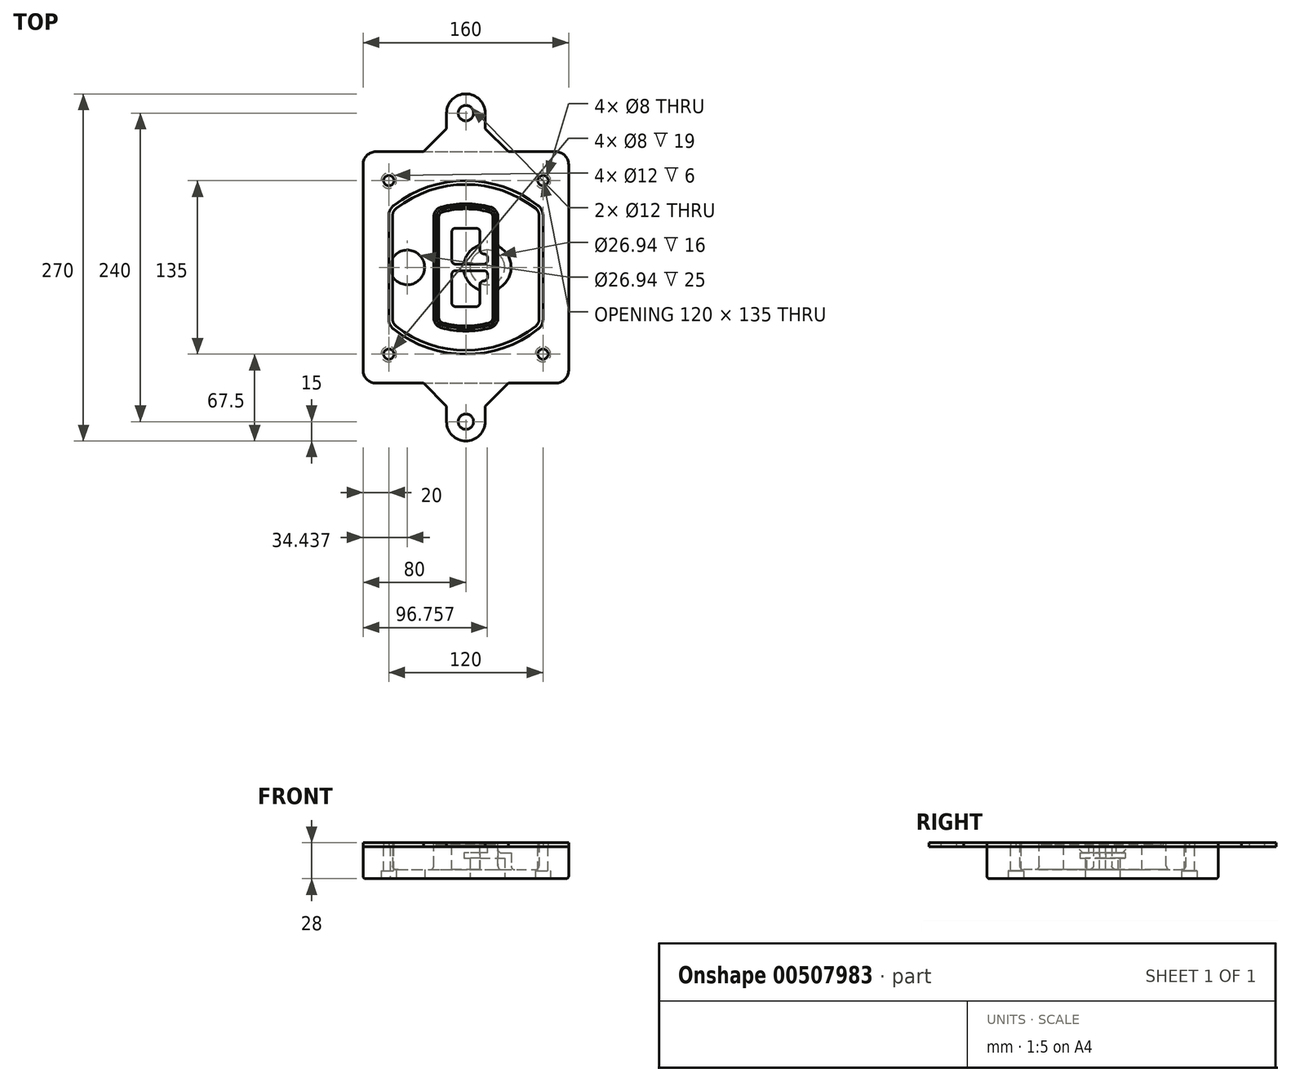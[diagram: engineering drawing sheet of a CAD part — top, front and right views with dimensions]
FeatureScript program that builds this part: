
annotation { "Feature Type Name" : "Feature", "Feature Type Description" : "" }
export const myFeature = defineFeature(function(context is Context, id is Id, definition is map)
    precondition{}
    {
        {
            var Q0;
            Q0=qCreatedBy(makeId("Top.planeOp"),FACE);
            var sketch = newSketch(context, id + "F0", { "sketchPlane" : qUnion([Q0])});
            skPoint(sketch, "E0.rect.middle", {"position": v(0, 0) * mm});
            skLineSegment(sketch, "E1.bottom", {"start": v(-70, -90) * mm, "end": v(70, -90) * mm});
            skLineSegment(sketch, "E1.top", {"start": v(-70, 90) * mm, "end": v(70, 90) * mm});
            skLineSegment(sketch, "E1.left", {"start": v(-80, -80) * mm, "end": v(-80, 80) * mm});
            skLineSegment(sketch, "E1.right", {"start": v(80, -80) * mm, "end": v(80, 80) * mm});
            skLineSegment(sketch, "E2", {"start": v(-80, 90) * mm, "end": v(80, -90) * mm, "construction": true});
            skLineSegment(sketch, "E3", {"start": v(80, 90) * mm, "end": v(-80, -90) * mm, "construction": true});
            skCircle(sketch, "E4", {"center": v(-60, 67.5) * mm, "radius": 4 * mm});
            skCircle(sketch, "E5", {"center": v(60, 67.5) * mm, "radius": 4 * mm});
            skCircle(sketch, "E6", {"center": v(60, -67.5) * mm, "radius": 4 * mm});
            skCircle(sketch, "E7", {"center": v(-60, -67.5) * mm, "radius": 4 * mm});
            skLineSegment(sketch, "E8", {"start": v(-60, 67.5) * mm, "end": v(60, 67.5) * mm, "construction": true});
            skLineSegment(sketch, "E9", {"start": v(60, 67.5) * mm, "end": v(60, -67.5) * mm, "construction": true});
            skLineSegment(sketch, "E10", {"start": v(60, -67.5) * mm, "end": v(-60, -67.5) * mm, "construction": true});
            skLineSegment(sketch, "E11", {"start": v(-60, -67.5) * mm, "end": v(-60, 67.5) * mm, "construction": true});
            skLineSegment(sketch, "E12", {"start": v(-60, 40.3) * mm, "end": v(-60, -40.3) * mm});
            skLineSegment(sketch, "E13", {"start": v(60, 40.3) * mm, "end": v(60, -40.3) * mm});
            skArc(sketch, "E14", {"start": v(56.15, 48.18) * mm, "mid": v(0, 67.5) * mm, "end": v(-56.15, 48.18) * mm});
            skArc(sketch, "E15", {"start": v(-56.15, -48.18) * mm, "mid": v(0, -67.5) * mm, "end": v(56.15, -48.18) * mm});
            skLineSegment(sketch, "E16", {"start": v(-60, 0) * mm, "end": v(60, 0) * mm, "construction": true});
            skPoint(sketch, "E17.visualSharp", {"position": v(-60, -45) * mm});
            skArc(sketch, "E17.filletArc", {"start": v(-60, -40.3) * mm, "mid": v(-58.99, -44.68) * mm, "end": v(-56.15, -48.18) * mm});
            skPoint(sketch, "E18.visualSharp", {"position": v(-60, 45) * mm});
            skArc(sketch, "E18.filletArc", {"start": v(-56.15, 48.18) * mm, "mid": v(-58.99, 44.68) * mm, "end": v(-60, 40.3) * mm});
            skPoint(sketch, "E19.visualSharp", {"position": v(60, 45) * mm});
            skArc(sketch, "E19.filletArc", {"start": v(60, 40.3) * mm, "mid": v(58.99, 44.68) * mm, "end": v(56.15, 48.18) * mm});
            skPoint(sketch, "E20.visualSharp", {"position": v(60, -45) * mm});
            skArc(sketch, "E20.filletArc", {"start": v(56.15, -48.18) * mm, "mid": v(58.99, -44.68) * mm, "end": v(60, -40.3) * mm});
            skPoint(sketch, "E21.visualSharp", {"position": v(-80, 90) * mm});
            skArc(sketch, "E21.filletArc", {"start": v(-70, 90) * mm, "mid": v(-77.07, 87.07) * mm, "end": v(-80, 80) * mm});
            skPoint(sketch, "E22.visualSharp", {"position": v(80, 90) * mm});
            skArc(sketch, "E22.filletArc", {"start": v(80, 80) * mm, "mid": v(77.07, 87.07) * mm, "end": v(70, 90) * mm});
            skPoint(sketch, "E23.visualSharp", {"position": v(80, -90) * mm});
            skArc(sketch, "E23.filletArc", {"start": v(70, -90) * mm, "mid": v(77.07, -87.07) * mm, "end": v(80, -80) * mm});
            skPoint(sketch, "E24.visualSharp", {"position": v(-80, -90) * mm});
            skArc(sketch, "E24.filletArc", {"start": v(-80, -80) * mm, "mid": v(-77.07, -87.07) * mm, "end": v(-70, -90) * mm});
            skArc(sketch, "E25.0", {"start": v(57, 40.3) * mm, "mid": v(56.3, 43.36) * mm, "end": v(54.3, 45.81) * mm});
            skLineSegment(sketch, "E25.1", {"start": v(57, 40.3) * mm, "end": v(57, -40.3) * mm});
            skArc(sketch, "E25.2", {"start": v(54.3, -45.81) * mm, "mid": v(56.3, -43.36) * mm, "end": v(57, -40.3) * mm});
            skArc(sketch, "E25.3", {"start": v(-54.3, -45.81) * mm, "mid": v(0, -64.5) * mm, "end": v(54.3, -45.81) * mm});
            skArc(sketch, "E25.4", {"start": v(-57, -40.3) * mm, "mid": v(-56.3, -43.36) * mm, "end": v(-54.3, -45.81) * mm});
            skArc(sketch, "E25.5", {"start": v(54.3, 45.81) * mm, "mid": v(0, 64.5) * mm, "end": v(-54.3, 45.81) * mm});
            skLineSegment(sketch, "E25.6", {"start": v(-57, 40.3) * mm, "end": v(-57, -40.3) * mm});
            skArc(sketch, "E25.7", {"start": v(-54.3, 45.81) * mm, "mid": v(-56.3, 43.36) * mm, "end": v(-57, 40.3) * mm});
            skArc(sketch, "E26.0", {"start": v(-58.62, 51.33) * mm, "mid": v(-62.58, 46.43) * mm, "end": v(-64, 40.3) * mm});
            skArc(sketch, "E26.1", {"start": v(58.62, 51.33) * mm, "mid": v(0, 71.5) * mm, "end": v(-58.62, 51.33) * mm});
            skArc(sketch, "E26.2", {"start": v(64, 40.3) * mm, "mid": v(62.58, 46.43) * mm, "end": v(58.62, 51.33) * mm});
            skLineSegment(sketch, "E26.3", {"start": v(64, 40.3) * mm, "end": v(64, -40.3) * mm});
            skArc(sketch, "E26.4", {"start": v(58.62, -51.33) * mm, "mid": v(62.58, -46.43) * mm, "end": v(64, -40.3) * mm});
            skLineSegment(sketch, "E26.5", {"start": v(-64, 40.3) * mm, "end": v(-64, -40.3) * mm});
            skArc(sketch, "E26.6", {"start": v(-58.62, -51.33) * mm, "mid": v(0, -71.5) * mm, "end": v(58.62, -51.33) * mm});
            skArc(sketch, "E26.7", {"start": v(-64, -40.3) * mm, "mid": v(-62.58, -46.43) * mm, "end": v(-58.62, -51.33) * mm});
            skSolve(sketch);
        }
        {
            var Q0;
            Q0=makeQuery(id+"F0.imprint","IMPRINT",FACE,{"disambiguationData":[TD([[makeQuery(id+"F0.imprint","IMPRINT",EDGE,{"derivedFrom":sQuery(id+"F0.wireOp",EDGE,"E1.bottom")}),1.0]])]});
            var Q1;
            Q1=makeQuery(id+"F0.imprint","IMPRINT",FACE,{"disambiguationData":[TD([[makeQuery(id+"F0.imprint","IMPRINT",EDGE,{"derivedFrom":sQuery(id+"F0.wireOp",EDGE,"E12")}),1.0]])]});
            var Q2;
            Q2=makeQuery(id+"F0.imprint","IMPRINT",FACE,{"disambiguationData":[TD([[makeQuery(id+"F0.imprint","IMPRINT",EDGE,{"derivedFrom":sQuery(id+"F0.wireOp",EDGE,"E25.0")}),1.0]])]});
            var Q3;
            Q3=makeQuery(id+"F0.imprint","IMPRINT",FACE,{"disambiguationData":[TD([[makeQuery(id+"F0.imprint","IMPRINT",EDGE,{"derivedFrom":sQuery(id+"F0.wireOp",EDGE,"E12")}),-1.0]])]});
            extrude(context, id + "F1", {"entities" : qUnion([Q0, Q1, Q2, Q3]), "oppositeDirection" : true, "depth" : 25 * mm});
        }
        {
            var Q0;
            Q0=makeQuery(id+"F0.imprint","IMPRINT",FACE,{"disambiguationData":[TD([[makeQuery(id+"F0.imprint","IMPRINT",EDGE,{"derivedFrom":sQuery(id+"F0.wireOp",EDGE,"E12")}),1.0]])]});
            extrude(context, id + "F2", {"entities" : qUnion([Q0]), "operationType" : NewBodyOperationType.ADD, "depth" : 3 * mm});
        }
        {
            var Q0;
            Q0=makeQuery(id+"F0.imprint","IMPRINT",FACE,{"disambiguationData":[TD([[makeQuery(id+"F0.imprint","IMPRINT",EDGE,{"derivedFrom":sQuery(id+"F0.wireOp",EDGE,"E25.0")}),1.0]])]});
            extrude(context, id + "F3", {"entities" : qUnion([Q0]), "operationType" : NewBodyOperationType.REMOVE, "oppositeDirection" : true, "depth" : 18 * mm});
        }
        {
            var Q0;
            Q0=makeQuery(id+"F2.opExtrude","CAP_FACE",FACE,{"disambiguationData":[OSD([sQuery(id+"F0.wireOp",EDGE,"E12"),sQuery(id+"F0.wireOp",EDGE,"E13"),sQuery(id+"F0.wireOp",EDGE,"E14"),sQuery(id+"F0.wireOp",EDGE,"E15"),sQuery(id+"F0.wireOp",EDGE,"E17.filletArc"),sQuery(id+"F0.wireOp",EDGE,"E18.filletArc"),sQuery(id+"F0.wireOp",EDGE,"E19.filletArc"),sQuery(id+"F0.wireOp",EDGE,"E20.filletArc"),sQuery(id+"F0.wireOp",EDGE,"E25.0"),sQuery(id+"F0.wireOp",EDGE,"E25.1"),sQuery(id+"F0.wireOp",EDGE,"E25.2"),sQuery(id+"F0.wireOp",EDGE,"E25.3"),sQuery(id+"F0.wireOp",EDGE,"E25.4"),sQuery(id+"F0.wireOp",EDGE,"E25.5"),sQuery(id+"F0.wireOp",EDGE,"E25.6"),sQuery(id+"F0.wireOp",EDGE,"E25.7")])],"isStart":false});
            var sketch = newSketch(context, id + "F4", { "sketchPlane" : qUnion([Q0])});
            skArc(sketch, "E27.0", {"start": v(-19.08, -46.97) * mm, "mid": v(0, -49.5) * mm, "end": v(19.08, -46.97) * mm});
            skArc(sketch, "E28.0", {"start": v(19.08, 46.97) * mm, "mid": v(0, 49.5) * mm, "end": v(-19.08, 46.97) * mm});
            skLineSegment(sketch, "E29", {"start": v(-25, 39.25) * mm, "end": v(-25, -39.25) * mm});
            skLineSegment(sketch, "E30", {"start": v(25, 39.25) * mm, "end": v(25, -39.25) * mm});
            skLineSegment(sketch, "E31", {"start": v(-25, 45.1) * mm, "end": v(25, 45.1) * mm, "construction": true});
            skLineSegment(sketch, "E32", {"start": v(-25, -45.1) * mm, "end": v(25, -45.1) * mm, "construction": true});
            skPoint(sketch, "E33.visualSharp", {"position": v(-25, 45.1) * mm});
            skArc(sketch, "E33.filletArc", {"start": v(-19.08, 46.97) * mm, "mid": v(-23.35, 44.11) * mm, "end": v(-25, 39.25) * mm});
            skPoint(sketch, "E34.visualSharp", {"position": v(25, 45.1) * mm});
            skArc(sketch, "E34.filletArc", {"start": v(25, 39.25) * mm, "mid": v(23.35, 44.11) * mm, "end": v(19.08, 46.97) * mm});
            skPoint(sketch, "E35.visualSharp", {"position": v(25, -45.1) * mm});
            skArc(sketch, "E35.filletArc", {"start": v(19.08, -46.97) * mm, "mid": v(23.35, -44.11) * mm, "end": v(25, -39.25) * mm});
            skPoint(sketch, "E36.visualSharp", {"position": v(-25, -45.1) * mm});
            skArc(sketch, "E36.filletArc", {"start": v(-25, -39.25) * mm, "mid": v(-23.35, -44.11) * mm, "end": v(-19.08, -46.97) * mm});
            skArc(sketch, "E37.0", {"start": v(54.3, 45.81) * mm, "mid": v(0, 64.5) * mm, "end": v(-54.3, 45.81) * mm});
            skArc(sketch, "E37.1", {"start": v(-54.3, 45.81) * mm, "mid": v(-56.3, 43.36) * mm, "end": v(-57, 40.3) * mm});
            skLineSegment(sketch, "E37.2", {"start": v(-57, 40.3) * mm, "end": v(-57, -40.3) * mm});
            skArc(sketch, "E37.3", {"start": v(-57, -40.3) * mm, "mid": v(-56.3, -43.36) * mm, "end": v(-54.3, -45.81) * mm});
            skArc(sketch, "E37.4", {"start": v(-54.3, -45.81) * mm, "mid": v(0, -64.5) * mm, "end": v(54.3, -45.81) * mm});
            skArc(sketch, "E37.5", {"start": v(54.3, -45.81) * mm, "mid": v(56.3, -43.36) * mm, "end": v(57, -40.3) * mm});
            skLineSegment(sketch, "E37.6", {"start": v(57, 40.3) * mm, "end": v(57, -40.3) * mm});
            skArc(sketch, "E37.7", {"start": v(57, 40.3) * mm, "mid": v(56.3, 43.36) * mm, "end": v(54.3, 45.81) * mm});
            skLineSegment(sketch, "E38.0", {"start": v(23, 39.25) * mm, "end": v(23, -39.25) * mm});
            skArc(sketch, "E38.1", {"start": v(18.56, -45.04) * mm, "mid": v(21.76, -42.9) * mm, "end": v(23, -39.25) * mm});
            skArc(sketch, "E38.2", {"start": v(-18.56, -45.04) * mm, "mid": v(0, -47.5) * mm, "end": v(18.56, -45.04) * mm});
            skArc(sketch, "E38.3", {"start": v(-23, -39.25) * mm, "mid": v(-21.76, -42.9) * mm, "end": v(-18.56, -45.04) * mm});
            skLineSegment(sketch, "E38.4", {"start": v(-23, 39.25) * mm, "end": v(-23, -39.25) * mm});
            skArc(sketch, "E38.5", {"start": v(23, 39.25) * mm, "mid": v(21.76, 42.9) * mm, "end": v(18.56, 45.04) * mm});
            skArc(sketch, "E38.6", {"start": v(-18.56, 45.04) * mm, "mid": v(-21.76, 42.9) * mm, "end": v(-23, 39.25) * mm});
            skArc(sketch, "E38.7", {"start": v(18.56, 45.04) * mm, "mid": v(0, 47.5) * mm, "end": v(-18.56, 45.04) * mm});
            skArc(sketch, "E39.0", {"start": v(21, 39.25) * mm, "mid": v(20.18, 41.68) * mm, "end": v(18.04, 43.1) * mm});
            skLineSegment(sketch, "E39.1", {"start": v(21, 39.25) * mm, "end": v(21, -39.25) * mm});
            skArc(sketch, "E39.2", {"start": v(18.04, -43.1) * mm, "mid": v(20.18, -41.68) * mm, "end": v(21, -39.25) * mm});
            skArc(sketch, "E39.3", {"start": v(-18.04, -43.1) * mm, "mid": v(0, -45.5) * mm, "end": v(18.04, -43.1) * mm});
            skArc(sketch, "E39.4", {"start": v(-21, -39.25) * mm, "mid": v(-20.18, -41.68) * mm, "end": v(-18.04, -43.1) * mm});
            skArc(sketch, "E39.5", {"start": v(18.04, 43.1) * mm, "mid": v(0, 45.5) * mm, "end": v(-18.04, 43.1) * mm});
            skLineSegment(sketch, "E39.6", {"start": v(-21, 39.25) * mm, "end": v(-21, -39.25) * mm});
            skArc(sketch, "E39.7", {"start": v(-18.04, 43.1) * mm, "mid": v(-20.18, 41.68) * mm, "end": v(-21, 39.25) * mm});
            skLineSegment(sketch, "E40", {"start": v(-25, 0) * mm, "end": v(25, 0) * mm, "construction": true});
            skLineSegment(sketch, "E41", {"start": v(-11, 5.5) * mm, "end": v(-11, 27.5) * mm});
            skLineSegment(sketch, "E42", {"start": v(-8, 30.5) * mm, "end": v(8, 30.5) * mm});
            skLineSegment(sketch, "E43", {"start": v(11, 27.5) * mm, "end": v(11, 13.5) * mm});
            skLineSegment(sketch, "E44", {"start": v(14, 10.5) * mm, "end": v(14, 10.5) * mm});
            skLineSegment(sketch, "E45", {"start": v(17, 7.5) * mm, "end": v(17, 5.5) * mm});
            skLineSegment(sketch, "E46", {"start": v(14, 2.5) * mm, "end": v(-8, 2.5) * mm});
            skPoint(sketch, "E47.visualSharp", {"position": v(-11, 30.5) * mm});
            skArc(sketch, "E47.filletArc", {"start": v(-8, 30.5) * mm, "mid": v(-10.12, 29.62) * mm, "end": v(-11, 27.5) * mm});
            skPoint(sketch, "E48.visualSharp", {"position": v(11, 30.5) * mm});
            skArc(sketch, "E48.filletArc", {"start": v(11, 27.5) * mm, "mid": v(10.12, 29.62) * mm, "end": v(8, 30.5) * mm});
            skPoint(sketch, "E49.visualSharp", {"position": v(11, 10.5) * mm});
            skArc(sketch, "E49.filletArc", {"start": v(11, 13.5) * mm, "mid": v(11.88, 11.38) * mm, "end": v(14, 10.5) * mm});
            skPoint(sketch, "E50.visualSharp", {"position": v(17, 10.5) * mm});
            skArc(sketch, "E50.filletArc", {"start": v(17, 7.5) * mm, "mid": v(16.12, 9.62) * mm, "end": v(14, 10.5) * mm});
            skPoint(sketch, "E51.visualSharp", {"position": v(17, 2.5) * mm});
            skArc(sketch, "E51.filletArc", {"start": v(14, 2.5) * mm, "mid": v(16.12, 3.38) * mm, "end": v(17, 5.5) * mm});
            skPoint(sketch, "E52.visualSharp", {"position": v(-11, 2.5) * mm});
            skArc(sketch, "E52.filletArc", {"start": v(-11, 5.5) * mm, "mid": v(-10.12, 3.38) * mm, "end": v(-8, 2.5) * mm});
            skLineSegment(sketch, "E53.0.MirrorCS", {"start": v(14, -2.5) * mm, "end": v(-8, -2.5) * mm});
            skArc(sketch, "E54.0.MirrorCS", {"start": v(-11, -5.5) * mm, "mid": v(-10.12, -3.38) * mm, "end": v(-8, -2.5) * mm});
            skLineSegment(sketch, "E55.0.MirrorCS", {"start": v(-11, -5.5) * mm, "end": v(-11, -27.5) * mm});
            skArc(sketch, "E56.0.MirrorCS", {"start": v(-8, -30.5) * mm, "mid": v(-10.12, -29.62) * mm, "end": v(-11, -27.5) * mm});
            skLineSegment(sketch, "E57.0.MirrorCS", {"start": v(-8, -30.5) * mm, "end": v(8, -30.5) * mm});
            skArc(sketch, "E58.0.MirrorCS", {"start": v(11, -27.5) * mm, "mid": v(10.12, -29.62) * mm, "end": v(8, -30.5) * mm});
            skLineSegment(sketch, "E59.0.MirrorCS", {"start": v(11, -27.5) * mm, "end": v(11, -13.5) * mm});
            skArc(sketch, "E60.0.MirrorCS", {"start": v(11, -13.5) * mm, "mid": v(11.88, -11.38) * mm, "end": v(14, -10.5) * mm});
            skArc(sketch, "E61.0.MirrorCS", {"start": v(17, -7.5) * mm, "mid": v(16.12, -9.62) * mm, "end": v(14, -10.5) * mm});
            skLineSegment(sketch, "E62.0.MirrorCS", {"start": v(17, -7.5) * mm, "end": v(17, -5.5) * mm});
            skArc(sketch, "E63.0.MirrorCS", {"start": v(14, -2.5) * mm, "mid": v(16.12, -3.38) * mm, "end": v(17, -5.5) * mm});
            skSolve(sketch);
        }
        {
            var Q0;
            Q0=makeQuery(id+"F4.imprint","IMPRINT",FACE,{"disambiguationData":[TD([[makeQuery(id+"F4.imprint","IMPRINT",EDGE,{"derivedFrom":sQuery(id+"F4.wireOp",EDGE,"E27.0")}),1.0]])]});
            var Q1;
            Q1=makeQuery(id+"F4.imprint","IMPRINT",FACE,{"disambiguationData":[TD([[makeQuery(id+"F4.imprint","IMPRINT",EDGE,{"derivedFrom":sQuery(id+"F4.wireOp",EDGE,"E38.0")}),-1.0]])]});
            var Q2;
            Q2=makeQuery(id+"F4.imprint","IMPRINT",FACE,{"disambiguationData":[TD([[makeQuery(id+"F4.imprint","IMPRINT",EDGE,{"derivedFrom":sQuery(id+"F4.wireOp",EDGE,"E39.0")}),1.0]])]});
            extrude(context, id + "F5", {"entities" : qUnion([Q0, Q1, Q2]), "operationType" : NewBodyOperationType.ADD, "endBound" : BoundingType.UP_TO_NEXT, "oppositeDirection" : true, "depth" : 25 * mm});
        }
        {
            var Q0;
            Q0=makeQuery(id+"F4.imprint","IMPRINT",FACE,{"disambiguationData":[TD([[makeQuery(id+"F4.imprint","IMPRINT",EDGE,{"derivedFrom":sQuery(id+"F4.wireOp",EDGE,"E38.0")}),-1.0]])]});
            extrude(context, id + "F6", {"entities" : qUnion([Q0]), "operationType" : NewBodyOperationType.REMOVE, "oppositeDirection" : true, "depth" : 2 * mm});
        }
        {
            var Q0;
            Q0=makeQuery(id+"F1.opExtrude","CAP_FACE",FACE,{"disambiguationData":[OSD([sQuery(id+"F0.wireOp",EDGE,"E1.bottom"),sQuery(id+"F0.wireOp",EDGE,"E1.top"),sQuery(id+"F0.wireOp",EDGE,"E1.left"),sQuery(id+"F0.wireOp",EDGE,"E1.right"),sQuery(id+"F0.wireOp",EDGE,"E4"),sQuery(id+"F0.wireOp",EDGE,"E5"),sQuery(id+"F0.wireOp",EDGE,"E6"),sQuery(id+"F0.wireOp",EDGE,"E7"),sQuery(id+"F0.wireOp",EDGE,"E21.filletArc"),sQuery(id+"F0.wireOp",EDGE,"E22.filletArc"),sQuery(id+"F0.wireOp",EDGE,"E23.filletArc"),sQuery(id+"F0.wireOp",EDGE,"E24.filletArc")])],"isStart":false});
            var sketch = newSketch(context, id + "F7", { "sketchPlane" : qUnion([Q0])});
            skCircle(sketch, "E64", {"center": v(16.76, 0) * mm, "radius": 13.47 * mm});
            skCircle(sketch, "E65", {"center": v(-45.56, 0) * mm, "radius": 13.47 * mm});
            skLineSegment(sketch, "E66", {"start": v(80, 0) * mm, "end": v(-80, 0) * mm});
            skCircle(sketch, "E67", {"center": v(16.76, 0) * mm, "radius": 18.47 * mm});
            skCircle(sketch, "E68", {"center": v(60, -67.5) * mm, "radius": 6 * mm});
            skCircle(sketch, "E69", {"center": v(-60, -67.5) * mm, "radius": 6 * mm});
            skCircle(sketch, "E70", {"center": v(-60, 67.5) * mm, "radius": 6 * mm});
            skCircle(sketch, "E71", {"center": v(60, 67.5) * mm, "radius": 6 * mm});
            skSolve(sketch);
        }
        {
            var Q0;
            {var subQ1=sQuery(id+"F7.wireOp",EDGE,"E66");var subQ4=sQuery(id+"F7.wireOp",EDGE,"E64");var subQ6=makeQuery(id+"F7.imprint","INTERSECT",VERTEX,{"disambiguationData":[OD(0.0)],"derivedFrom":[subQ4,subQ1]});Q0=makeQuery(id+"F7.imprint","IMPRINT",FACE,{"disambiguationData":[TD([[makeQuery(id+"F7.imprint","IMPRINT",EDGE,{"disambiguationData":[TD([[subQ6,-1.0]])],"derivedFrom":subQ4}),-1.0]])]});}
            var Q1;
            {var subQ0=sQuery(id+"F7.wireOp",EDGE,"E66");var subQ1=sQuery(id+"F7.wireOp",EDGE,"E64");var subQ3=makeQuery(id+"F7.imprint","INTERSECT",VERTEX,{"disambiguationData":[OD(0.0)],"derivedFrom":[subQ1,subQ0]});Q1=makeQuery(id+"F7.imprint","IMPRINT",FACE,{"disambiguationData":[TD([[makeQuery(id+"F7.imprint","IMPRINT",EDGE,{"disambiguationData":[TD([[subQ3,-1.0]])],"derivedFrom":subQ1}),1.0]])]});}
            var Q2;
            {var subQ0=sQuery(id+"F7.wireOp",EDGE,"E66");var subQ1=sQuery(id+"F7.wireOp",EDGE,"E64");var subQ3=makeQuery(id+"F7.imprint","INTERSECT",VERTEX,{"disambiguationData":[OD(0.0)],"derivedFrom":[subQ1,subQ0]});Q2=makeQuery(id+"F7.imprint","IMPRINT",FACE,{"disambiguationData":[TD([[makeQuery(id+"F7.imprint","IMPRINT",EDGE,{"disambiguationData":[TD([[subQ3,1.0]])],"derivedFrom":subQ1}),1.0]])]});}
            var Q3;
            {var subQ1=sQuery(id+"F7.wireOp",EDGE,"E66");var subQ4=sQuery(id+"F7.wireOp",EDGE,"E64");var subQ6=makeQuery(id+"F7.imprint","INTERSECT",VERTEX,{"disambiguationData":[OD(0.0)],"derivedFrom":[subQ4,subQ1]});Q3=makeQuery(id+"F7.imprint","IMPRINT",FACE,{"disambiguationData":[TD([[makeQuery(id+"F7.imprint","IMPRINT",EDGE,{"disambiguationData":[TD([[subQ6,1.0]])],"derivedFrom":subQ4}),-1.0]])]});}
            extrude(context, id + "F8", {"entities" : qUnion([Q0, Q1, Q2, Q3]), "operationType" : NewBodyOperationType.ADD, "oppositeDirection" : true, "depth" : 20 * mm});
        }
        {
            var Q0;
            {var subQ0=sQuery(id+"F7.wireOp",EDGE,"E66");var subQ1=sQuery(id+"F7.wireOp",EDGE,"E64");var subQ3=makeQuery(id+"F7.imprint","INTERSECT",VERTEX,{"disambiguationData":[OD(0.0)],"derivedFrom":[subQ1,subQ0]});Q0=makeQuery(id+"F7.imprint","IMPRINT",FACE,{"disambiguationData":[TD([[makeQuery(id+"F7.imprint","IMPRINT",EDGE,{"disambiguationData":[TD([[subQ3,-1.0]])],"derivedFrom":subQ1}),1.0]])]});}
            var Q1;
            {var subQ0=sQuery(id+"F7.wireOp",EDGE,"E66");var subQ1=sQuery(id+"F7.wireOp",EDGE,"E64");var subQ3=makeQuery(id+"F7.imprint","INTERSECT",VERTEX,{"disambiguationData":[OD(0.0)],"derivedFrom":[subQ1,subQ0]});Q1=makeQuery(id+"F7.imprint","IMPRINT",FACE,{"disambiguationData":[TD([[makeQuery(id+"F7.imprint","IMPRINT",EDGE,{"disambiguationData":[TD([[subQ3,1.0]])],"derivedFrom":subQ1}),1.0]])]});}
            extrude(context, id + "F9", {"entities" : qUnion([Q0, Q1]), "operationType" : NewBodyOperationType.REMOVE, "oppositeDirection" : true, "depth" : 16 * mm});
        }
        {
            var Q0;
            {var subQ0=sQuery(id+"F7.wireOp",EDGE,"E66");var subQ1=sQuery(id+"F7.wireOp",EDGE,"E65");var subQ3=makeQuery(id+"F7.imprint","INTERSECT",VERTEX,{"disambiguationData":[OD(0.0)],"derivedFrom":[subQ1,subQ0]});Q0=makeQuery(id+"F7.imprint","IMPRINT",FACE,{"disambiguationData":[TD([[makeQuery(id+"F7.imprint","IMPRINT",EDGE,{"disambiguationData":[TD([[subQ3,-1.0]])],"derivedFrom":subQ1}),1.0]])]});}
            var Q1;
            {var subQ0=sQuery(id+"F7.wireOp",EDGE,"E66");var subQ1=sQuery(id+"F7.wireOp",EDGE,"E65");var subQ3=makeQuery(id+"F7.imprint","INTERSECT",VERTEX,{"disambiguationData":[OD(0.0)],"derivedFrom":[subQ1,subQ0]});Q1=makeQuery(id+"F7.imprint","IMPRINT",FACE,{"disambiguationData":[TD([[makeQuery(id+"F7.imprint","IMPRINT",EDGE,{"disambiguationData":[TD([[subQ3,1.0]])],"derivedFrom":subQ1}),1.0]])]});}
            extrude(context, id + "F10", {"entities" : qUnion([Q0, Q1]), "operationType" : NewBodyOperationType.REMOVE, "oppositeDirection" : true, "depth" : 25 * mm});
        }
        {
            var Q0;
            Q0=makeQuery(id+"F7.imprint","IMPRINT",FACE,{"disambiguationData":[TD([[makeQuery(id+"F7.imprint","IMPRINT",EDGE,{"derivedFrom":sQuery(id+"F7.wireOp",EDGE,"E68")}),1.0]])]});
            var Q1;
            Q1=makeQuery(id+"F7.imprint","IMPRINT",FACE,{"disambiguationData":[TD([[makeQuery(id+"F7.imprint","IMPRINT",EDGE,{"derivedFrom":makeQuery(id+"F1.opExtrude","CAP_EDGE",EDGE,{"disambiguationData":[OSD([sQuery(id+"F0.wireOp",EDGE,"E5")])],"isStart":false})}),-1.0]])]});
            var Q2;
            Q2=makeQuery(id+"F7.imprint","IMPRINT",FACE,{"disambiguationData":[TD([[makeQuery(id+"F7.imprint","IMPRINT",EDGE,{"derivedFrom":sQuery(id+"F7.wireOp",EDGE,"E69")}),1.0]])]});
            var Q3;
            Q3=makeQuery(id+"F7.imprint","IMPRINT",FACE,{"disambiguationData":[TD([[makeQuery(id+"F7.imprint","IMPRINT",EDGE,{"derivedFrom":makeQuery(id+"F1.opExtrude","CAP_EDGE",EDGE,{"disambiguationData":[OSD([sQuery(id+"F0.wireOp",EDGE,"E4")])],"isStart":false})}),-1.0]])]});
            var Q4;
            Q4=makeQuery(id+"F7.imprint","IMPRINT",FACE,{"disambiguationData":[TD([[makeQuery(id+"F7.imprint","IMPRINT",EDGE,{"derivedFrom":sQuery(id+"F7.wireOp",EDGE,"E70")}),1.0]])]});
            var Q5;
            Q5=makeQuery(id+"F7.imprint","IMPRINT",FACE,{"disambiguationData":[TD([[makeQuery(id+"F7.imprint","IMPRINT",EDGE,{"derivedFrom":makeQuery(id+"F1.opExtrude","CAP_EDGE",EDGE,{"disambiguationData":[OSD([sQuery(id+"F0.wireOp",EDGE,"E7")])],"isStart":false})}),-1.0]])]});
            var Q6;
            Q6=makeQuery(id+"F7.imprint","IMPRINT",FACE,{"disambiguationData":[TD([[makeQuery(id+"F7.imprint","IMPRINT",EDGE,{"derivedFrom":sQuery(id+"F7.wireOp",EDGE,"E71")}),1.0]])]});
            var Q7;
            Q7=makeQuery(id+"F7.imprint","IMPRINT",FACE,{"disambiguationData":[TD([[makeQuery(id+"F7.imprint","IMPRINT",EDGE,{"derivedFrom":makeQuery(id+"F1.opExtrude","CAP_EDGE",EDGE,{"disambiguationData":[OSD([sQuery(id+"F0.wireOp",EDGE,"E6")])],"isStart":false})}),-1.0]])]});
            extrude(context, id + "F11", {"entities" : qUnion([Q0, Q1, Q2, Q3, Q4, Q5, Q6, Q7]), "operationType" : NewBodyOperationType.REMOVE, "oppositeDirection" : true, "depth" : 6 * mm});
        }
        {
            var Q0;
            Q0=makeQuery(id+"F9.boolean.opBoolean","COPY",FACE,{"derivedFrom":makeQuery(id+"F9.opExtrude","CAP_FACE",FACE,{"disambiguationData":[OSD([sQuery(id+"F7.wireOp",EDGE,"E64")])],"isStart":false})});
            var sketch = newSketch(context, id + "F12", { "sketchPlane" : qUnion([Q0])});
            skArc(sketch, "E72.0", {"start": v(11, 17.55) * mm, "mid": v(2.57, 11.82) * mm, "end": v(-1.54, 2.5) * mm});
            skArc(sketch, "E72.1", {"start": v(-1.54, -2.5) * mm, "mid": v(2.57, -11.82) * mm, "end": v(11, -17.55) * mm});
            skLineSegment(sketch, "E73", {"start": v(-1.54, -2.5) * mm, "end": v(14, -2.5) * mm});
            skLineSegment(sketch, "E74.0", {"start": v(14, 2.5) * mm, "end": v(-1.54, 2.5) * mm});
            skArc(sketch, "E74.1", {"start": v(14, 2.5) * mm, "mid": v(16.12, 3.38) * mm, "end": v(17, 5.5) * mm});
            skLineSegment(sketch, "E74.2", {"start": v(17, 7.5) * mm, "end": v(17, 5.5) * mm});
            skArc(sketch, "E74.3", {"start": v(17, 7.5) * mm, "mid": v(16.12, 9.62) * mm, "end": v(14, 10.5) * mm});
            skArc(sketch, "E74.4", {"start": v(11, 13.5) * mm, "mid": v(11.88, 11.38) * mm, "end": v(14, 10.5) * mm});
            skLineSegment(sketch, "E74.5", {"start": v(11, 17.55) * mm, "end": v(11, 13.5) * mm});
            skLineSegment(sketch, "E74.7", {"start": v(14, -2.5) * mm, "end": v(-1.54, -2.5) * mm});
            skArc(sketch, "E74.8", {"start": v(14, -2.5) * mm, "mid": v(16.12, -3.38) * mm, "end": v(17, -5.5) * mm});
            skLineSegment(sketch, "E74.9", {"start": v(17, -7.5) * mm, "end": v(17, -5.5) * mm});
            skArc(sketch, "E74.10", {"start": v(17, -7.5) * mm, "mid": v(16.12, -9.62) * mm, "end": v(14, -10.5) * mm});
            skArc(sketch, "E74.11", {"start": v(11, -13.5) * mm, "mid": v(11.88, -11.38) * mm, "end": v(14, -10.5) * mm});
            skLineSegment(sketch, "E74.12", {"start": v(11, -17.55) * mm, "end": v(11, -13.5) * mm});
            skPoint(sketch, "E75.orphan", {"position": v(11, -27.5) * mm});
            skPoint(sketch, "E76.orphan", {"position": v(-8, -2.5) * mm});
            skPoint(sketch, "E77.orphan", {"position": v(-8, 2.5) * mm});
            skPoint(sketch, "E78.orphan", {"position": v(11, 27.5) * mm});
            skSolve(sketch);
        }
        {
            var Q0;
            {var subQ7=sQuery(id+"F12.wireOp",EDGE,"E72.0");var subQ14=sQuery(id+"F12.wireOp",EDGE,"E72.1");var subQ16=sQuery(id+"F12.wireOp",EDGE,"E74.1");var subQ18=sQuery(id+"F12.wireOp",EDGE,"E74.8");Q0=qUnion([makeQuery(id+"F12.imprint","IMPRINT",FACE,{"disambiguationData":[TD([[makeQuery(id+"F12.imprint","IMPRINT",EDGE,{"derivedFrom":subQ7}),1.0]])]}),makeQuery(id+"F12.imprint","IMPRINT",FACE,{"disambiguationData":[TD([[makeQuery(id+"F12.imprint","IMPRINT",EDGE,{"derivedFrom":subQ14}),1.0]])]}),makeQuery(id+"F12.imprint","IMPRINT",FACE,{"disambiguationData":[TD([[makeQuery(id+"F12.imprint","IMPRINT",EDGE,{"derivedFrom":subQ16}),1.0]])]}),makeQuery(id+"F12.imprint","IMPRINT",FACE,{"disambiguationData":[TD([[makeQuery(id+"F12.imprint","IMPRINT",EDGE,{"derivedFrom":subQ18}),-1.0]])]})]);}
            var Q1;
            Q1=makeQuery(id+"F5.boolean.opBoolean","SPLIT",FACE,{"disambiguationData":[TD([makeQuery(id+"F5.opExtrude","SWEPT_FACE",FACE,{"disambiguationData":[OSD([sQuery(id+"F4.wireOp",EDGE,"E41")])]})])],"derivedFrom":makeQuery(id+"F3.boolean.opBoolean","COPY",FACE,{"derivedFrom":makeQuery(id+"F3.opExtrude","CAP_FACE",FACE,{"disambiguationData":[OSD([sQuery(id+"F0.wireOp",EDGE,"E25.0"),sQuery(id+"F0.wireOp",EDGE,"E25.1"),sQuery(id+"F0.wireOp",EDGE,"E25.2"),sQuery(id+"F0.wireOp",EDGE,"E25.3"),sQuery(id+"F0.wireOp",EDGE,"E25.4"),sQuery(id+"F0.wireOp",EDGE,"E25.5"),sQuery(id+"F0.wireOp",EDGE,"E25.6"),sQuery(id+"F0.wireOp",EDGE,"E25.7")])],"isStart":false})})});
            extrude(context, id + "F13", {"entities" : qUnion([Q0]), "operationType" : NewBodyOperationType.REMOVE, "endBound" : BoundingType.UP_TO_SURFACE, "endBoundEntityFace" : qUnion([Q1]), "depth" : 25 * mm});
        }
        {
            var Q0;
            Q0=makeQuery(id+"F3.boolean.opBoolean","COPY",EDGE,{"derivedFrom":makeQuery(id+"F3.opExtrude","CAP_EDGE",EDGE,{"disambiguationData":[OSD([sQuery(id+"F0.wireOp",EDGE,"E25.6")])],"isStart":false})});
            var Q1;
            Q1=makeQuery(id+"F8.boolean.opBoolean","INTERSECT",EDGE,{"derivedFrom":[makeQuery(id+"F5.opExtrude","SWEPT_FACE",FACE,{"disambiguationData":[OSD([sQuery(id+"F4.wireOp",EDGE,"E30")])]}),makeQuery(id+"F8.opExtrude","CAP_FACE",FACE,{"disambiguationData":[OSD([sQuery(id+"F7.wireOp",EDGE,"E67")])],"isStart":false})]});
            var Q2;
            Q2=makeQuery(id+"F8.boolean.opBoolean","INTERSECT",EDGE,{"disambiguationData":[OD(1.0)],"derivedFrom":[makeQuery(id+"F5.opExtrude","SWEPT_FACE",FACE,{"disambiguationData":[OSD([sQuery(id+"F4.wireOp",EDGE,"E30")])]}),makeQuery(id+"F8.opExtrude","SWEPT_FACE",FACE,{"disambiguationData":[OSD([sQuery(id+"F7.wireOp",EDGE,"E67")])]})]});
            var Q3;
            {var subQ0=sQuery(id+"F4.wireOp",EDGE,"E30");Q3=makeQuery(id+"F8.boolean.opBoolean","SPLIT",EDGE,{"disambiguationData":[TD([makeQuery(id+"F5.opExtrude","SWEPT_FACE",FACE,{"disambiguationData":[OSD([sQuery(id+"F4.wireOp",EDGE,"E35.filletArc")])]})])],"derivedFrom":makeQuery(id+"F5.opExtrude","CAP_EDGE",EDGE,{"disambiguationData":[OSD([subQ0])],"isStart":false})});}
            var Q4;
            {var subQ0=sQuery(id+"F0.wireOp",EDGE,"E25.7");var subQ1=sQuery(id+"F0.wireOp",EDGE,"E25.1");var subQ2=sQuery(id+"F0.wireOp",EDGE,"E25.6");var subQ3=sQuery(id+"F0.wireOp",EDGE,"E25.5");var subQ4=sQuery(id+"F0.wireOp",EDGE,"E25.4");var subQ5=sQuery(id+"F0.wireOp",EDGE,"E25.0");var subQ6=sQuery(id+"F0.wireOp",EDGE,"E25.2");var subQ7=sQuery(id+"F0.wireOp",EDGE,"E25.3");Q4=makeQuery(id+"F8.boolean.opBoolean","INTERSECT",EDGE,{"derivedFrom":[makeQuery(id+"F5.boolean.opBoolean","SPLIT",FACE,{"disambiguationData":[TD([makeQuery(id+"F2.opExtrude","SWEPT_FACE",FACE,{"disambiguationData":[OSD([subQ5])]})])],"derivedFrom":makeQuery(id+"F3.boolean.opBoolean","COPY",FACE,{"derivedFrom":makeQuery(id+"F3.opExtrude","CAP_FACE",FACE,{"disambiguationData":[OSD([subQ5,subQ1,subQ6,subQ7,subQ4,subQ3,subQ2,subQ0])],"isStart":false})})}),makeQuery(id+"F8.opExtrude","SWEPT_FACE",FACE,{"disambiguationData":[OSD([sQuery(id+"F7.wireOp",EDGE,"E67")])]})]});}
            var Q5;
            Q5=makeQuery(id+"F8.boolean.opBoolean","INTERSECT",EDGE,{"disambiguationData":[OD(0.0)],"derivedFrom":[makeQuery(id+"F5.opExtrude","SWEPT_FACE",FACE,{"disambiguationData":[OSD([sQuery(id+"F4.wireOp",EDGE,"E30")])]}),makeQuery(id+"F8.opExtrude","SWEPT_FACE",FACE,{"disambiguationData":[OSD([sQuery(id+"F7.wireOp",EDGE,"E67")])]})]});
            fillet(context, id + "F14", {"entities" : qUnion([Q0, Q1, Q2, Q3, Q4, Q5]), "radius" : 3 * mm, "tangentPropagation" : true, "allowEdgeOverflow" : false});
        }
        {
            var Q0;
            Q0=makeQuery(id+"F1.opExtrude","CAP_EDGE",EDGE,{"disambiguationData":[OSD([sQuery(id+"F0.wireOp",EDGE,"E1.bottom")])],"isStart":false});
            fillet(context, id + "F15", {"entities" : qUnion([Q0]), "radius" : 2 * mm, "tangentPropagation" : true, "allowEdgeOverflow" : false});
        }
        {
            var Q0;
            {var subQ0=sQuery(id+"F0.wireOp",EDGE,"E21.filletArc");var subQ1=sQuery(id+"F0.wireOp",EDGE,"E7");var subQ2=sQuery(id+"F0.wireOp",EDGE,"E6");var subQ3=sQuery(id+"F0.wireOp",EDGE,"E5");var subQ4=sQuery(id+"F0.wireOp",EDGE,"E4");var subQ5=sQuery(id+"F0.wireOp",EDGE,"E22.filletArc");var subQ6=sQuery(id+"F0.wireOp",EDGE,"E1.bottom");var subQ7=sQuery(id+"F0.wireOp",EDGE,"E1.right");var subQ8=sQuery(id+"F0.wireOp",EDGE,"E1.top");var subQ9=sQuery(id+"F0.wireOp",EDGE,"E1.left");var subQ10=sQuery(id+"F0.wireOp",EDGE,"E23.filletArc");var subQ11=sQuery(id+"F0.wireOp",EDGE,"E24.filletArc");Q0=makeQuery(id+"F2.boolean.opBoolean","SPLIT",FACE,{"disambiguationData":[TD([makeQuery(id+"F1.opExtrude","SWEPT_FACE",FACE,{"disambiguationData":[OSD([subQ6])]})])],"derivedFrom":makeQuery(id+"F1.opExtrude","CAP_FACE",FACE,{"disambiguationData":[OSD([subQ6,subQ8,subQ9,subQ7,subQ4,subQ3,subQ2,subQ1,subQ0,subQ5,subQ10,subQ11])],"isStart":true})});}
            var sketch = newSketch(context, id + "F16", { "sketchPlane" : qUnion([Q0])});
            skLineSegment(sketch, "E79.0.0", {"start": v(70, 90) * mm, "end": v(-70, 90) * mm});
            skArc(sketch, "E79.0.1", {"start": v(-70, 90) * mm, "mid": v(-77.07, 87.07) * mm, "end": v(-80, 80) * mm});
            skLineSegment(sketch, "E79.0.2", {"start": v(-80, 80) * mm, "end": v(-80, -80) * mm});
            skArc(sketch, "E79.0.3", {"start": v(-80, -80) * mm, "mid": v(-77.07, -87.07) * mm, "end": v(-70, -90) * mm});
            skLineSegment(sketch, "E79.0.4", {"start": v(-70, -90) * mm, "end": v(70, -90) * mm});
            skArc(sketch, "E79.0.5", {"start": v(70, -90) * mm, "mid": v(77.07, -87.07) * mm, "end": v(80, -80) * mm});
            skLineSegment(sketch, "E79.0.6", {"start": v(80, -80) * mm, "end": v(80, 80) * mm});
            skArc(sketch, "E79.0.7", {"start": v(80, 80) * mm, "mid": v(77.07, 87.07) * mm, "end": v(70, 90) * mm});
            skLineSegment(sketch, "E80", {"start": v(0, 90) * mm, "end": v(0, 120) * mm, "construction": true});
            skCircle(sketch, "E81", {"center": v(0, 120) * mm, "radius": 6 * mm});
            skLineSegment(sketch, "E82", {"start": v(-15, 120) * mm, "end": v(-15, 108) * mm});
            skArc(sketch, "E83", {"start": v(15, 120) * mm, "mid": v(0, 135) * mm, "end": v(-15, 120) * mm});
            skLineSegment(sketch, "E84", {"start": v(15, 108) * mm, "end": v(15, 120) * mm});
            skLineSegment(sketch, "E85", {"start": v(-15, 108) * mm, "end": v(-33, 90) * mm});
            skLineSegment(sketch, "E86", {"start": v(15, 108) * mm, "end": v(33, 90) * mm});
            skLineSegment(sketch, "E87", {"start": v(-80, 0) * mm, "end": v(80, 0) * mm, "construction": true});
            skLineSegment(sketch, "E88.MirrorCS", {"start": v(15, -108) * mm, "end": v(15, -120) * mm});
            skLineSegment(sketch, "E89.MirrorCS", {"start": v(-15, -120) * mm, "end": v(-15, -108) * mm});
            skLineSegment(sketch, "E90.MirrorCS", {"start": v(15, -108) * mm, "end": v(33, -90) * mm});
            skLineSegment(sketch, "E91.MirrorCS", {"start": v(-15, -108) * mm, "end": v(-33, -90) * mm});
            skLineSegment(sketch, "E92.MirrorCS", {"start": v(0, -90) * mm, "end": v(0, -120) * mm, "construction": true});
            skCircle(sketch, "E93.MirrorC", {"center": v(0, -120) * mm, "radius": 6 * mm});
            skArc(sketch, "E94.MirrorCS", {"start": v(15, -120) * mm, "mid": v(0, -135) * mm, "end": v(-15, -120) * mm});
            skSolve(sketch);
        }
        {
            var Q0;
            Q0=makeQuery(id+"F16.imprint","IMPRINT",FACE,{"disambiguationData":[TD([[makeQuery(id+"F16.imprint","IMPRINT",EDGE,{"derivedFrom":sQuery(id+"F16.wireOp",EDGE,"E88.MirrorCS")}),-1.0]])]});
            var Q1;
            Q1=makeQuery(id+"F16.imprint","IMPRINT",FACE,{"disambiguationData":[TD([[makeQuery(id+"F16.imprint","IMPRINT",EDGE,{"derivedFrom":sQuery(id+"F16.wireOp",EDGE,"E81")}),-1.0]])]});
            var Q2;
            {var subQ1=sQuery(id+"F16.wireOp",EDGE,"E79.0.1");Q2=makeQuery(id+"F16.imprint","IMPRINT",FACE,{"disambiguationData":[TD([[makeQuery(id+"F16.imprint","IMPRINT",EDGE,{"derivedFrom":subQ1}),1.0]])]});}
            var Q3;
            Q3=makeQuery(id+"F2.opExtrude","CAP_FACE",FACE,{"disambiguationData":[OSD([sQuery(id+"F0.wireOp",EDGE,"E12"),sQuery(id+"F0.wireOp",EDGE,"E13"),sQuery(id+"F0.wireOp",EDGE,"E14"),sQuery(id+"F0.wireOp",EDGE,"E15"),sQuery(id+"F0.wireOp",EDGE,"E17.filletArc"),sQuery(id+"F0.wireOp",EDGE,"E18.filletArc"),sQuery(id+"F0.wireOp",EDGE,"E19.filletArc"),sQuery(id+"F0.wireOp",EDGE,"E20.filletArc"),sQuery(id+"F0.wireOp",EDGE,"E25.0"),sQuery(id+"F0.wireOp",EDGE,"E25.1"),sQuery(id+"F0.wireOp",EDGE,"E25.2"),sQuery(id+"F0.wireOp",EDGE,"E25.3"),sQuery(id+"F0.wireOp",EDGE,"E25.4"),sQuery(id+"F0.wireOp",EDGE,"E25.5"),sQuery(id+"F0.wireOp",EDGE,"E25.6"),sQuery(id+"F0.wireOp",EDGE,"E25.7")])],"isStart":false});
            extrude(context, id + "F17", {"entities" : qUnion([Q0, Q1, Q2]), "endBound" : BoundingType.UP_TO_SURFACE, "endBoundEntityFace" : qUnion([Q3]), "depth" : 25 * mm});
        }
    });
